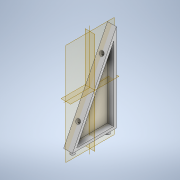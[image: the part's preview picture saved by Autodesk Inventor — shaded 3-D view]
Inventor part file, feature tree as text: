
AUTODESK INVENTOR PART (.ipt)
format: ipt  version: 2022.4 (Build 264492010, 492A)  size: 139,776 bytes
history: native  units: mm
features: extrude x4, sketch x4
ambient origin geometry x8: Origin, YZ Plane, XZ Plane, XY Plane, X Axis, Y Axis, Z Axis, Center Point
bodies: Solid1 (feature_tree)
feature tree (8):
  extrude  "Extrusion1"  Depth=100.0mm
  extrude  "Extrusion2"  Depth=3.0mm
  extrude  "Extrusion3"  Depth=5.0mm
  extrude  "Extrusion4"  Depth=10.0mm
  sketch  "Sketch2"  dims[d0=50.0mm d1=100.0mm]
  sketch  "Sketch4"  dims[d2=10.0mm d3=0.0mm d8=3.0mm]
  sketch  "Sketch5"  dims[d9=7.0mm d10=0.0mm d11=5.0mm]
  sketch  "Sketch8"  dims[d12=5.0mm d13=20.0mm d15=40.0mm d16=10.0mm d18=10.0mm d20=5.0mm d21=0.0mm d31=111.803399mm d32=5.0mm d34=30.0mm d35=7.0mm d36=0.0mm]
